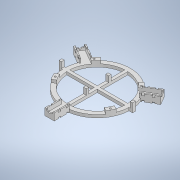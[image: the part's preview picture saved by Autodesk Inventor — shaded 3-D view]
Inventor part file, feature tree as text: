
AUTODESK INVENTOR PART (.ipt)
format: ipt  version: 2020.2 (Build 242310000, 310)  size: 584,192 bytes
history: native  units: mm
features: sketch x9, extrude x8, projected_geometry x7, plane x2, pattern_circular x1, hole x1
ambient origin geometry x8: Origin, YZ Plane, XZ Plane, XY Plane, X Axis, Y Axis, Z Axis, Center Point
bodies: Solid1 (feature_tree)
feature tree (28):
  extrude  "Extrusion1"  Depth=100.0mm
  extrude  "Extrusion7"  Depth=5.0mm TaperAngle=0.0deg
  extrude  "Extrusion8"  Depth=2.0mm
  extrude  "Extrusion5"  Depth=5.0mm
  extrude  "Extrusion6"  Depth=2.0mm
  plane  "Work Plane1"
  plane  "Work Plane2"
  extrude  "Extrusion12"  Depth=13.5mm TaperAngle=0.0deg
  extrude  "Extrusion13"  Depth=3.0mm
  pattern_circular  "Circular Pattern3"  [2 undecoded]
  extrude  "Extrusion9"  Depth=0.5mm
  hole  "Hole1"  [1 undecoded]
  sketch  "Sketch1"  dims[d0=114.0mm d1=100.0mm]
  sketch  "Sketch6"  dims[d10=16.0mm d20=5.0mm d21=0.0mm]
  sketch  "Sketch7"  dims[d46=27.0mm d47=2.0mm]
  sketch  "Sketch8"  dims[d48=7.0mm d49=0.0mm d51=5.0mm]
  sketch  "Sketch9"  dims[d53=9.0mm d54=2.0mm]
  sketch  "Sketch10"  dims[d55=2.0mm d56=13.5mm d57=0.0mm]
  projected_geometry  "Projected Loop1"
  sketch  "Sketch11"  dims[d61=107.0mm d62=3.0mm]
  projected_geometry  "Projected Loop2"
  sketch  "Sketch14"  dims[d63=3.0mm]
  projected_geometry  "Projected Loop5"
  sketch  "Sketch15"  dims[d64=3.0mm d65=3.0mm d66=35.0mm d67=35.0mm d68=25.0mm d69=25.0mm d71=32.0mm d90=30.0mm d92=360.0deg d94=5.0mm d95=30.0mm d96=360.0deg d98=118.0mm d99=34.0mm d100=5.0mm d101=4.2mm d102=5.0mm d103=5.0mm d104=0.0mm d105=118.0mm d106=34.0mm d107=4.0mm d108=4.0mm d109=0.2mm d110=10.0mm d111=0.0mm d112=0.2mm d113=13.0mm d114=8.0mm d115=8.0mm d116=13.0mm d117=5.0mm d118=0.0mm d119=6.0mm d120=6.0mm d121=18.0mm d122=4.8mm d123=90.0deg d124=5.0mm d125=20.594885mm d136=7.0mm d137=22.0mm d138=3.0mm d139=3.6mm d140=0.0mm d141=3.6mm d142=0.0mm d143=2.0mm d144=45.0deg d126=0.5mm d127=0.872665mm d128=0.5mm d129=0.872665mm]
  projected_geometry  "Projected Loop6"
  projected_geometry  "Projected Loop7"
  projected_geometry  "Projected Loop8"
  projected_geometry  "Projected Loop9"
note: 3 required parameter values undecoded (feature->parameter linkage not recoverable at this tier; creation-order binding heuristic only, values carry confidence <= 0.55)
